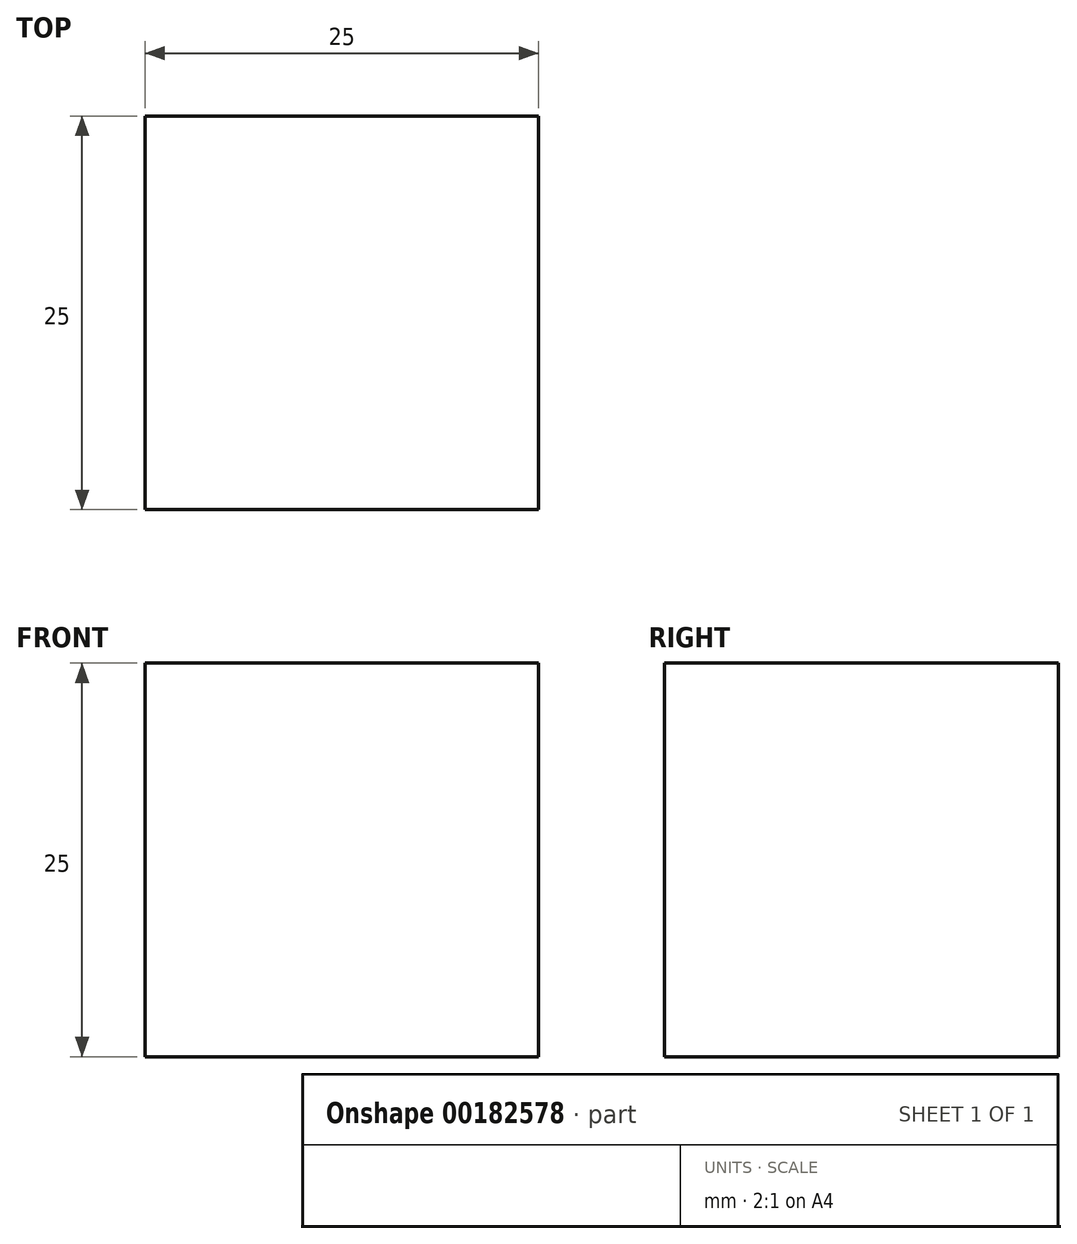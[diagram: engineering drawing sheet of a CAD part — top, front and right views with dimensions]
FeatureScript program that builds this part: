
annotation { "Feature Type Name" : "Feature", "Feature Type Description" : "" }
export const myFeature = defineFeature(function(context is Context, id is Id, definition is map)
    precondition{}
    {
        {
            var Q0;
            Q0=qCreatedBy(makeId("Top.planeOp"),FACE);
            var sketch = newSketch(context, id + "F0", { "sketchPlane" : qUnion([Q0])});
            skLineSegment(sketch, "E0.bottom", {"start": v(0, 0) * mm, "end": v(25, 0) * mm});
            skLineSegment(sketch, "E0.top", {"start": v(0, 25) * mm, "end": v(25, 25) * mm});
            skLineSegment(sketch, "E0.left", {"start": v(0, 0) * mm, "end": v(0, 25) * mm});
            skLineSegment(sketch, "E0.right", {"start": v(25, 0) * mm, "end": v(25, 25) * mm});
            skSolve(sketch);
        }
        {
            var Q0;
            Q0=qSketchRegion(id+"F0",true);
            extrude(context, id + "F1", {"entities" : qUnion([Q0]), "depth" : 25 * mm});
        }
    });
